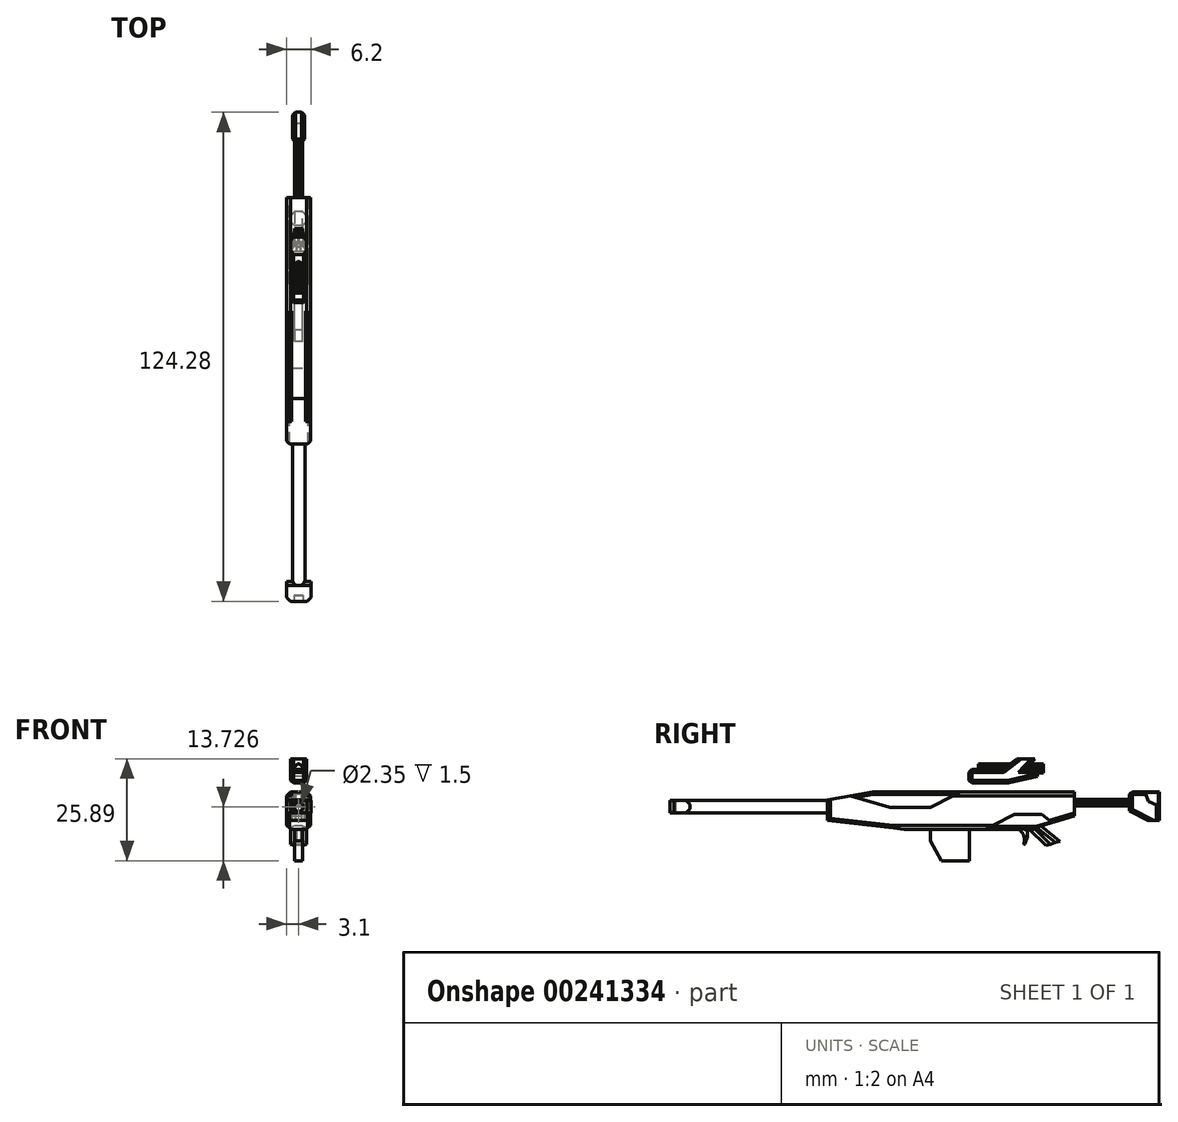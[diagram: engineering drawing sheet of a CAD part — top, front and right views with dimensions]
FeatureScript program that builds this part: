
annotation { "Feature Type Name" : "Feature", "Feature Type Description" : "" }
export const myFeature = defineFeature(function(context is Context, id is Id, definition is map)
    precondition{}
    {
        {
            var Q0;
            Q0=qCreatedBy(makeId("Right.planeOp"),FACE);
            var sketch = newSketch(context, id + "F0", { "sketchPlane" : qUnion([Q0])});
            skLineSegment(sketch, "E0.bottom", {"start": v(13.03, -2.2) * mm, "end": v(-18.93, -2.2) * mm});
            skLineSegment(sketch, "E0.top", {"start": v(24.37, 7.34) * mm, "end": v(-26.77, 7.34) * mm});
            skLineSegment(sketch, "E0.left", {"start": v(24.37, 1.22) * mm, "end": v(24.37, 7.34) * mm});
            skLineSegment(sketch, "E0.right", {"start": v(-38.28, 0) * mm, "end": v(-38.28, 5.3) * mm});
            skLineSegment(sketch, "E1.bottom", {"start": v(24.37, 5.38) * mm, "end": v(38.43, 5.38) * mm});
            skLineSegment(sketch, "E1.top", {"start": v(24.37, 3.77) * mm, "end": v(38.43, 3.77) * mm});
            skLineSegment(sketch, "E1.left", {"start": v(24.37, 5.38) * mm, "end": v(24.37, 3.77) * mm});
            skLineSegment(sketch, "E1.right", {"start": v(38.43, 5.38) * mm, "end": v(38.43, 3.77) * mm});
            skLineSegment(sketch, "E2.bottom", {"start": v(38.43, 7.34) * mm, "end": v(46, 7.34) * mm});
            skLineSegment(sketch, "E2.top", {"start": v(43.12, 0) * mm, "end": v(46, 0) * mm});
            skLineSegment(sketch, "E2.left", {"start": v(38.43, 7.34) * mm, "end": v(38.43, 2.48) * mm});
            skLineSegment(sketch, "E2.right", {"start": v(46, 7.34) * mm, "end": v(46, 0) * mm});
            skLineSegment(sketch, "E3", {"start": v(38.43, 2.48) * mm, "end": v(43.12, 0) * mm});
            skLineSegment(sketch, "E4", {"start": v(24.37, 1.22) * mm, "end": v(13.03, -2.2) * mm});
            skLineSegment(sketch, "E5", {"start": v(-26.77, 7.34) * mm, "end": v(-38.28, 5.3) * mm});
            skLineSegment(sketch, "E6", {"start": v(-18.93, -2.2) * mm, "end": v(-38.28, 0) * mm});
            skLineSegment(sketch, "E7", {"start": v(15.95, -1.32) * mm, "end": v(20.76, -5.24) * mm});
            skLineSegment(sketch, "E8", {"start": v(20.76, -5.24) * mm, "end": v(17.18, -6.32) * mm});
            skLineSegment(sketch, "E9", {"start": v(17.18, -6.32) * mm, "end": v(13.03, -2.2) * mm});
            skLineSegment(sketch, "E10", {"start": v(18.7, -0.49) * mm, "end": v(16.14, 1.57) * mm});
            skLineSegment(sketch, "E11", {"start": v(16.14, 1.57) * mm, "end": v(9.2, 1.57) * mm});
            skLineSegment(sketch, "E12", {"start": v(9.2, 1.57) * mm, "end": v(1.75, -2.2) * mm});
            skLineSegment(sketch, "E13", {"start": v(-4.55, 7.34) * mm, "end": v(-12.13, 3.37) * mm});
            skLineSegment(sketch, "E14", {"start": v(-12.13, 3.37) * mm, "end": v(-22.4, 3.37) * mm});
            skLineSegment(sketch, "E15", {"start": v(-22.4, 3.37) * mm, "end": v(-32.53, 6.32) * mm});
            skLineSegment(sketch, "E16", {"start": v(42.21, 7.34) * mm, "end": v(43.25, 4.9) * mm});
            skLineSegment(sketch, "E17", {"start": v(43.25, 4.9) * mm, "end": v(46, 3.67) * mm});
            skLineSegment(sketch, "E18.bottom", {"start": v(14.98, 13) * mm, "end": v(11.83, 13) * mm});
            skLineSegment(sketch, "E18.top", {"start": v(7.66, 9.53) * mm, "end": v(-2.36, 9.53) * mm});
            skLineSegment(sketch, "E18.left", {"start": v(14.98, 13) * mm, "end": v(14.98, 11.27) * mm});
            skLineSegment(sketch, "E18.right", {"start": v(-2.36, 13) * mm, "end": v(-2.36, 9.53) * mm});
            skLineSegment(sketch, "E19", {"start": v(14.98, 11.27) * mm, "end": v(7.66, 9.53) * mm});
            skLineSegment(sketch, "E20", {"start": v(11.83, 13) * mm, "end": v(14.34, 15.7) * mm});
            skLineSegment(sketch, "E21", {"start": v(14.34, 15.7) * mm, "end": v(9.84, 15.7) * mm});
            skLineSegment(sketch, "E22", {"start": v(9.84, 15.7) * mm, "end": v(6.3, 13) * mm});
            skLineSegment(sketch, "E23", {"start": v(8.08, 14.35) * mm, "end": v(0, 14.35) * mm});
            skLineSegment(sketch, "E24", {"start": v(0, 14.35) * mm, "end": v(0, 13) * mm});
            skPoint(sketch, "E25.orphan", {"position": v(14.98, 9.53) * mm});
            skLineSegment(sketch, "E26.trimOffspring", {"start": v(6.3, 13) * mm, "end": v(-2.36, 13) * mm});
            skLineSegment(sketch, "E27", {"start": v(13.08, 14.35) * mm, "end": v(16.5, 14.35) * mm});
            skLineSegment(sketch, "E28", {"start": v(16.5, 14.35) * mm, "end": v(16.5, 12.14) * mm});
            skLineSegment(sketch, "E29", {"start": v(16.5, 12.14) * mm, "end": v(14.98, 12.14) * mm});
            skFitSpline(sketch, "E30", {"points": [v(11.9, -2.2) * mm, v(12.5, -3.65) * mm, v(11.65, -6.06) * mm, v(11.53, -3.7) * mm, v(10.58, -2.2) * mm, v(11.9, -2.2) * mm]});
            skSolve(sketch);
        }
        {
            var Q0;
            {var subQ5=sQuery(id+"F0.wireOp",EDGE,"E0.right");Q0=makeQuery(id+"F0.imprint","IMPRINT",FACE,{"disambiguationData":[TD([[makeQuery(id+"F0.imprint","IMPRINT",EDGE,{"derivedFrom":subQ5}),-1.0]])]});}
            extrude(context, id + "F1", {"entities" : qUnion([Q0]), "oppositeDirection" : true, "depth" : 3 * mm});
        }
        {
            var Q0;
            {var subQ5=sQuery(id+"F0.wireOp",EDGE,"E0.right");Q0=makeQuery(id+"F0.imprint","IMPRINT",FACE,{"disambiguationData":[TD([[makeQuery(id+"F0.imprint","IMPRINT",EDGE,{"derivedFrom":subQ5}),-1.0]])]});}
            extrude(context, id + "F2", {"entities" : qUnion([Q0]), "operationType" : NewBodyOperationType.ADD, "depth" : 3 * mm});
        }
        {
            var Q0;
            {var subQ0=sQuery(id+"F0.wireOp",EDGE,"E13");Q0=makeQuery(id+"F0.imprint","IMPRINT",FACE,{"disambiguationData":[TD([[makeQuery(id+"F0.imprint","IMPRINT",EDGE,{"derivedFrom":subQ0}),-1.0]])]});}
            extrude(context, id + "F3", {"entities" : qUnion([Q0]), "operationType" : NewBodyOperationType.ADD, "oppositeDirection" : true, "depth" : 2.5 * mm});
        }
        {
            var Q0;
            {var subQ0=sQuery(id+"F0.wireOp",EDGE,"E13");Q0=makeQuery(id+"F0.imprint","IMPRINT",FACE,{"disambiguationData":[TD([[makeQuery(id+"F0.imprint","IMPRINT",EDGE,{"derivedFrom":subQ0}),-1.0]])]});}
            extrude(context, id + "F4", {"entities" : qUnion([Q0]), "operationType" : NewBodyOperationType.ADD, "depth" : 2.5 * mm});
        }
        {
            var Q0;
            {var subQ0=sQuery(id+"F0.wireOp",EDGE,"E10");Q0=makeQuery(id+"F0.imprint","IMPRINT",FACE,{"disambiguationData":[TD([[makeQuery(id+"F0.imprint","IMPRINT",EDGE,{"derivedFrom":subQ0}),1.0]])]});}
            extrude(context, id + "F5", {"entities" : qUnion([Q0]), "operationType" : NewBodyOperationType.ADD, "depth" : 2.5 * mm});
        }
        {
            var Q0;
            {var subQ0=sQuery(id+"F0.wireOp",EDGE,"E10");Q0=makeQuery(id+"F0.imprint","IMPRINT",FACE,{"disambiguationData":[TD([[makeQuery(id+"F0.imprint","IMPRINT",EDGE,{"derivedFrom":subQ0}),1.0]])]});}
            extrude(context, id + "F6", {"entities" : qUnion([Q0]), "operationType" : NewBodyOperationType.ADD, "oppositeDirection" : true, "depth" : 2.5 * mm});
        }
        {
            var Q0;
            {var subQ2=sQuery(id+"F0.wireOp",EDGE,"E7");Q0=makeQuery(id+"F0.imprint","IMPRINT",FACE,{"disambiguationData":[TD([[makeQuery(id+"F0.imprint","IMPRINT",EDGE,{"derivedFrom":subQ2}),-1.0]])]});}
            extrude(context, id + "F7", {"entities" : qUnion([Q0]), "operationType" : NewBodyOperationType.ADD, "depth" : 2 * mm});
        }
        {
            var Q0;
            {var subQ2=sQuery(id+"F0.wireOp",EDGE,"E7");Q0=makeQuery(id+"F0.imprint","IMPRINT",FACE,{"disambiguationData":[TD([[makeQuery(id+"F0.imprint","IMPRINT",EDGE,{"derivedFrom":subQ2}),-1.0]])]});}
            extrude(context, id + "F8", {"entities" : qUnion([Q0]), "operationType" : NewBodyOperationType.ADD, "oppositeDirection" : true, "depth" : 2 * mm});
        }
        {
            var Q0;
            {var subQ0=sQuery(id+"F0.wireOp",EDGE,"E1.bottom");Q0=makeQuery(id+"F0.imprint","IMPRINT",FACE,{"disambiguationData":[TD([[makeQuery(id+"F0.imprint","IMPRINT",EDGE,{"derivedFrom":subQ0}),-1.0]])]});}
            extrude(context, id + "F9", {"entities" : qUnion([Q0]), "operationType" : NewBodyOperationType.ADD, "depth" : 1 * mm});
        }
        {
            var Q0;
            {var subQ0=sQuery(id+"F0.wireOp",EDGE,"E1.bottom");Q0=makeQuery(id+"F0.imprint","IMPRINT",FACE,{"disambiguationData":[TD([[makeQuery(id+"F0.imprint","IMPRINT",EDGE,{"derivedFrom":subQ0}),-1.0]])]});}
            extrude(context, id + "F10", {"entities" : qUnion([Q0]), "operationType" : NewBodyOperationType.ADD, "oppositeDirection" : true, "depth" : 1 * mm});
        }
        {
            var Q0;
            {var subQ7=sQuery(id+"F0.wireOp",EDGE,"E2.top");Q0=makeQuery(id+"F0.imprint","IMPRINT",FACE,{"disambiguationData":[TD([[makeQuery(id+"F0.imprint","IMPRINT",EDGE,{"derivedFrom":subQ7}),1.0]])]});}
            extrude(context, id + "F11", {"entities" : qUnion([Q0]), "operationType" : NewBodyOperationType.ADD, "depth" : 1.5 * mm});
        }
        {
            var Q0;
            {var subQ7=sQuery(id+"F0.wireOp",EDGE,"E2.top");Q0=makeQuery(id+"F0.imprint","IMPRINT",FACE,{"disambiguationData":[TD([[makeQuery(id+"F0.imprint","IMPRINT",EDGE,{"derivedFrom":subQ7}),1.0]])]});}
            extrude(context, id + "F12", {"entities" : qUnion([Q0]), "operationType" : NewBodyOperationType.ADD, "oppositeDirection" : true, "depth" : 1.5 * mm});
        }
        {
            var Q0;
            {var subQ3=sQuery(id+"F0.wireOp",EDGE,"E16");Q0=makeQuery(id+"F0.imprint","IMPRINT",FACE,{"disambiguationData":[TD([[makeQuery(id+"F0.imprint","IMPRINT",EDGE,{"derivedFrom":subQ3}),1.0]])]});}
            extrude(context, id + "F13", {"entities" : qUnion([Q0]), "operationType" : NewBodyOperationType.ADD, "depth" : 1 * mm});
        }
        {
            var Q0;
            {var subQ3=sQuery(id+"F0.wireOp",EDGE,"E16");Q0=makeQuery(id+"F0.imprint","IMPRINT",FACE,{"disambiguationData":[TD([[makeQuery(id+"F0.imprint","IMPRINT",EDGE,{"derivedFrom":subQ3}),1.0]])]});}
            extrude(context, id + "F14", {"entities" : qUnion([Q0]), "operationType" : NewBodyOperationType.ADD, "oppositeDirection" : true, "depth" : 1 * mm});
        }
        {
            var Q0;
            Q0=makeQuery(id+"F0.imprint","IMPRINT",FACE,{"disambiguationData":[TD([[makeQuery(id+"F0.imprint","IMPRINT",EDGE,{"derivedFrom":sQuery(id+"F0.wireOp",EDGE,"E18.bottom")}),1.0]])]});
            extrude(context, id + "F15", {"entities" : qUnion([Q0]), "depth" : 2 * mm});
        }
        {
            var Q0;
            Q0=makeQuery(id+"F0.imprint","IMPRINT",FACE,{"disambiguationData":[TD([[makeQuery(id+"F0.imprint","IMPRINT",EDGE,{"derivedFrom":sQuery(id+"F0.wireOp",EDGE,"E18.bottom")}),1.0]])]});
            extrude(context, id + "F16", {"entities" : qUnion([Q0]), "operationType" : NewBodyOperationType.ADD, "oppositeDirection" : true, "depth" : 2 * mm});
        }
        {
            var Q0;
            {var subQ3=sQuery(id+"F0.wireOp",EDGE,"E23");Q0=makeQuery(id+"F0.imprint","IMPRINT",FACE,{"disambiguationData":[TD([[makeQuery(id+"F0.imprint","IMPRINT",EDGE,{"derivedFrom":subQ3}),1.0]])]});}
            var Q1;
            {var subQ1=sQuery(id+"F0.wireOp",EDGE,"E18.bottom");Q1=makeQuery(id+"F0.imprint","IMPRINT",FACE,{"disambiguationData":[TD([[makeQuery(id+"F0.imprint","IMPRINT",EDGE,{"derivedFrom":subQ1}),-1.0]])]});}
            extrude(context, id + "F17", {"entities" : qUnion([Q0, Q1]), "operationType" : NewBodyOperationType.ADD, "depth" : 1 * mm});
        }
        {
            var Q0;
            {var subQ3=sQuery(id+"F0.wireOp",EDGE,"E23");Q0=makeQuery(id+"F0.imprint","IMPRINT",FACE,{"disambiguationData":[TD([[makeQuery(id+"F0.imprint","IMPRINT",EDGE,{"derivedFrom":subQ3}),1.0]])]});}
            var Q1;
            {var subQ1=sQuery(id+"F0.wireOp",EDGE,"E18.bottom");Q1=makeQuery(id+"F0.imprint","IMPRINT",FACE,{"disambiguationData":[TD([[makeQuery(id+"F0.imprint","IMPRINT",EDGE,{"derivedFrom":subQ1}),-1.0]])]});}
            extrude(context, id + "F18", {"entities" : qUnion([Q0, Q1]), "operationType" : NewBodyOperationType.ADD, "oppositeDirection" : true, "depth" : 1 * mm});
        }
        {
            var Q0;
            Q0=makeQuery(id+"F10.opExtrude","CAP_EDGE",EDGE,{"disambiguationData":[OSD([sQuery(id+"F0.wireOp",EDGE,"E1.bottom")])],"isStart":false});
            var Q1;
            Q1=makeQuery(id+"F16.opExtrude","CAP_EDGE",EDGE,{"disambiguationData":[OSD([sQuery(id+"F0.wireOp",EDGE,"E26.trimOffspring")])],"isStart":false});
            var Q2;
            Q2=makeQuery(id+"F15.opExtrude","CAP_EDGE",EDGE,{"disambiguationData":[OSD([sQuery(id+"F0.wireOp",EDGE,"E26.trimOffspring")])],"isStart":false});
            var Q3;
            Q3=makeQuery(id+"F9.opExtrude","CAP_EDGE",EDGE,{"disambiguationData":[OSD([sQuery(id+"F0.wireOp",EDGE,"E1.bottom")])],"isStart":false});
            var Q4;
            Q4=makeQuery(id+"F10.opExtrude","CAP_EDGE",EDGE,{"disambiguationData":[OSD([sQuery(id+"F0.wireOp",EDGE,"E1.top")])],"isStart":false});
            var Q5;
            Q5=makeQuery(id+"F9.opExtrude","CAP_EDGE",EDGE,{"disambiguationData":[OSD([sQuery(id+"F0.wireOp",EDGE,"E1.top")])],"isStart":false});
            var Q6;
            Q6=makeQuery(id+"F11.opExtrude","CAP_EDGE",EDGE,{"disambiguationData":[OSD([sQuery(id+"F0.wireOp",EDGE,"E2.bottom")])],"isStart":false});
            var Q7;
            Q7=makeQuery(id+"F12.opExtrude","CAP_EDGE",EDGE,{"disambiguationData":[OSD([sQuery(id+"F0.wireOp",EDGE,"E2.bottom")])],"isStart":false});
            var Q8;
            Q8=makeQuery(id+"F12.opExtrude","CAP_EDGE",EDGE,{"disambiguationData":[OSD([sQuery(id+"F0.wireOp",EDGE,"E3")])],"isStart":false});
            var Q9;
            Q9=makeQuery(id+"F11.opExtrude","CAP_EDGE",EDGE,{"disambiguationData":[OSD([sQuery(id+"F0.wireOp",EDGE,"E3")])],"isStart":false});
            var Q10;
            Q10=makeQuery(id+"F11.opExtrude","CAP_EDGE",EDGE,{"disambiguationData":[OSD([sQuery(id+"F0.wireOp",EDGE,"E2.right")])],"isStart":false});
            var Q11;
            Q11=makeQuery(id+"F12.opExtrude","CAP_EDGE",EDGE,{"disambiguationData":[OSD([sQuery(id+"F0.wireOp",EDGE,"E2.right")])],"isStart":false});
            var Q12;
            Q12=makeQuery(id+"F16.opExtrude","CAP_EDGE",EDGE,{"disambiguationData":[OSD([sQuery(id+"F0.wireOp",EDGE,"E19")])],"isStart":false});
            var Q13;
            Q13=makeQuery(id+"F15.opExtrude","CAP_EDGE",EDGE,{"disambiguationData":[OSD([sQuery(id+"F0.wireOp",EDGE,"E18.top")])],"isStart":false});
            var Q14;
            Q14=makeQuery(id+"F15.opExtrude","CAP_EDGE",EDGE,{"disambiguationData":[OSD([sQuery(id+"F0.wireOp",EDGE,"E19")])],"isStart":false});
            var Q15;
            Q15=makeQuery(id+"F15.opExtrude","CAP_EDGE",EDGE,{"disambiguationData":[OSD([sQuery(id+"F0.wireOp",EDGE,"E18.bottom")])],"isStart":false});
            var Q16;
            Q16=makeQuery(id+"F15.opExtrude","CAP_EDGE",EDGE,{"disambiguationData":[OSD([sQuery(id+"F0.wireOp",EDGE,"E20")])],"isStart":false});
            var Q17;
            Q17=makeQuery(id+"F15.opExtrude","CAP_EDGE",EDGE,{"disambiguationData":[OSD([sQuery(id+"F0.wireOp",EDGE,"E22")])],"isStart":false});
            var Q18;
            Q18=makeQuery(id+"F16.opExtrude","CAP_EDGE",EDGE,{"disambiguationData":[OSD([sQuery(id+"F0.wireOp",EDGE,"E18.top")])],"isStart":false});
            var Q19;
            Q19=makeQuery(id+"F16.opExtrude","CAP_EDGE",EDGE,{"disambiguationData":[OSD([sQuery(id+"F0.wireOp",EDGE,"E18.right")])],"isStart":false});
            var Q20;
            Q20=makeQuery(id+"F15.opExtrude","CAP_EDGE",EDGE,{"disambiguationData":[OSD([sQuery(id+"F0.wireOp",EDGE,"E18.right")])],"isStart":false});
            var Q21;
            {var subQ0=sQuery(id+"F0.wireOp",EDGE,"E26.trimOffspring");var subQ1=sQuery(id+"F0.wireOp",EDGE,"E18.right");Q21=makeQuery(id+"F16.boolean.opBoolean","MERGE",EDGE,{"derivedFrom":[makeQuery(id+"F15.opExtrude","SWEPT_EDGE",EDGE,{"disambiguationData":[OSD([subQ1,subQ0])]}),makeQuery(id+"F16.opExtrude","SWEPT_EDGE",EDGE,{"disambiguationData":[OSD([subQ1,subQ0])]})]});}
            var Q22;
            {var subQ0=sQuery(id+"F0.wireOp",EDGE,"E18.right");var subQ1=sQuery(id+"F0.wireOp",EDGE,"E18.top");Q22=makeQuery(id+"F16.boolean.opBoolean","MERGE",EDGE,{"derivedFrom":[makeQuery(id+"F15.opExtrude","SWEPT_EDGE",EDGE,{"disambiguationData":[OSD([subQ1,subQ0])]}),makeQuery(id+"F16.opExtrude","SWEPT_EDGE",EDGE,{"disambiguationData":[OSD([subQ1,subQ0])]})]});}
            var Q23;
            Q23=makeQuery(id+"F16.opExtrude","CAP_EDGE",EDGE,{"disambiguationData":[OSD([sQuery(id+"F0.wireOp",EDGE,"E20")])],"isStart":false});
            var Q24;
            Q24=makeQuery(id+"F16.opExtrude","CAP_EDGE",EDGE,{"disambiguationData":[OSD([sQuery(id+"F0.wireOp",EDGE,"E22")])],"isStart":false});
            var Q25;
            Q25=makeQuery(id+"F16.opExtrude","CAP_EDGE",EDGE,{"disambiguationData":[OSD([sQuery(id+"F0.wireOp",EDGE,"E18.bottom")])],"isStart":false});
            var Q26;
            {var subQ0=sQuery(id+"F0.wireOp",EDGE,"E2.left");var subQ1=sQuery(id+"F0.wireOp",EDGE,"E2.bottom");Q26=makeQuery(id+"F12.boolean.opBoolean","MERGE",EDGE,{"derivedFrom":[makeQuery(id+"F11.opExtrude","SWEPT_EDGE",EDGE,{"disambiguationData":[OSD([subQ1,subQ0])]}),makeQuery(id+"F12.opExtrude","SWEPT_EDGE",EDGE,{"disambiguationData":[OSD([subQ1,subQ0])]})]});}
            chamfer(context, id + "F19", {"entities" : qUnion([Q0, Q1, Q2, Q3, Q4, Q5, Q6, Q7, Q8, Q9, Q10, Q11, Q12, Q13, Q14, Q15, Q16, Q17, Q18, Q19, Q20, Q21, Q22, Q23, Q24, Q25, Q26]), "width" : 0.7 * mm, "tangentPropagation" : true});
        }
        {
            var Q0;
            Q0=makeQuery(id+"F12.opExtrude","CAP_EDGE",EDGE,{"disambiguationData":[OSD([sQuery(id+"F0.wireOp",EDGE,"E2.left")])],"isStart":false});
            var Q1;
            Q1=makeQuery(id+"F11.opExtrude","CAP_EDGE",EDGE,{"disambiguationData":[OSD([sQuery(id+"F0.wireOp",EDGE,"E2.left")])],"isStart":false});
            var Q2;
            Q2=makeQuery(id+"F3.opExtrude","CAP_EDGE",EDGE,{"disambiguationData":[OSD([sQuery(id+"F0.wireOp",EDGE,"E0.top")])],"isStart":false});
            var Q3;
            Q3=makeQuery(id+"F3.opExtrude","CAP_EDGE",EDGE,{"disambiguationData":[OSD([sQuery(id+"F0.wireOp",EDGE,"E5")])],"isStart":false});
            var Q4;
            Q4=makeQuery(id+"F4.opExtrude","CAP_EDGE",EDGE,{"disambiguationData":[OSD([sQuery(id+"F0.wireOp",EDGE,"E5")])],"isStart":false});
            var Q5;
            Q5=makeQuery(id+"F4.opExtrude","CAP_EDGE",EDGE,{"disambiguationData":[OSD([sQuery(id+"F0.wireOp",EDGE,"E0.top")])],"isStart":false});
            var Q6;
            Q6=makeQuery(id+"F1.opExtrude","CAP_EDGE",EDGE,{"disambiguationData":[OSD([sQuery(id+"F0.wireOp",EDGE,"E0.right")])],"isStart":false});
            var Q7;
            Q7=makeQuery(id+"F2.opExtrude","CAP_EDGE",EDGE,{"disambiguationData":[OSD([sQuery(id+"F0.wireOp",EDGE,"E0.right")])],"isStart":false});
            var Q8;
            Q8=makeQuery(id+"F1.opExtrude","CAP_EDGE",EDGE,{"disambiguationData":[OSD([sQuery(id+"F0.wireOp",EDGE,"E6")])],"isStart":false});
            var Q9;
            Q9=makeQuery(id+"F2.opExtrude","CAP_EDGE",EDGE,{"disambiguationData":[OSD([sQuery(id+"F0.wireOp",EDGE,"E6")])],"isStart":false});
            var Q10;
            Q10=makeQuery(id+"F6.opExtrude","CAP_EDGE",EDGE,{"disambiguationData":[OSD([sQuery(id+"F0.wireOp",EDGE,"E0.bottom")])],"isStart":false});
            var Q11;
            Q11=makeQuery(id+"F5.opExtrude","CAP_EDGE",EDGE,{"disambiguationData":[OSD([sQuery(id+"F0.wireOp",EDGE,"E0.bottom")])],"isStart":false});
            var Q12;
            Q12=makeQuery(id+"F1.opExtrude","CAP_EDGE",EDGE,{"disambiguationData":[OSD([sQuery(id+"F0.wireOp",EDGE,"E4")])],"isStart":false});
            var Q13;
            Q13=makeQuery(id+"F2.opExtrude","CAP_EDGE",EDGE,{"disambiguationData":[OSD([sQuery(id+"F0.wireOp",EDGE,"E4")])],"isStart":false});
            chamfer(context, id + "F20", {"entities" : qUnion([Q0, Q1, Q2, Q3, Q4, Q5, Q6, Q7, Q8, Q9, Q10, Q11, Q12, Q13]), "width" : 0.7 * mm, "tangentPropagation" : true});
        }
        {
            var Q0;
            Q0=makeQuery(id+"F1.opExtrude","CAP_EDGE",EDGE,{"disambiguationData":[OSD([sQuery(id+"F0.wireOp",EDGE,"E0.top")])],"isStart":false});
            var Q1;
            Q1=makeQuery(id+"F2.opExtrude","CAP_EDGE",EDGE,{"disambiguationData":[OSD([sQuery(id+"F0.wireOp",EDGE,"E0.top")])],"isStart":false});
            var Q2;
            Q2=makeQuery(id+"F1.opExtrude","CAP_EDGE",EDGE,{"disambiguationData":[OSD([sQuery(id+"F0.wireOp",EDGE,"E0.bottom")])],"isStart":false});
            var Q3;
            Q3=makeQuery(id+"F2.opExtrude","CAP_EDGE",EDGE,{"disambiguationData":[OSD([sQuery(id+"F0.wireOp",EDGE,"E0.bottom")])],"isStart":false});
            var Q4;
            Q4=makeQuery(id+"F8.opExtrude","CAP_EDGE",EDGE,{"disambiguationData":[OSD([sQuery(id+"F0.wireOp",EDGE,"E9")])],"isStart":false});
            var Q5;
            Q5=makeQuery(id+"F8.opExtrude","CAP_EDGE",EDGE,{"disambiguationData":[OSD([sQuery(id+"F0.wireOp",EDGE,"E7")])],"isStart":false});
            var Q6;
            Q6=makeQuery(id+"F7.opExtrude","CAP_EDGE",EDGE,{"disambiguationData":[OSD([sQuery(id+"F0.wireOp",EDGE,"E9")])],"isStart":false});
            var Q7;
            Q7=makeQuery(id+"F7.opExtrude","CAP_EDGE",EDGE,{"disambiguationData":[OSD([sQuery(id+"F0.wireOp",EDGE,"E7")])],"isStart":false});
            chamfer(context, id + "F21", {"entities" : qUnion([Q0, Q1, Q2, Q3, Q4, Q5, Q6, Q7]), "width" : 1 * mm, "tangentPropagation" : true});
        }
        {
            var Q0;
            Q0=makeQuery(id+"F18.opExtrude","CAP_EDGE",EDGE,{"disambiguationData":[OSD([sQuery(id+"F0.wireOp",EDGE,"E27")])],"isStart":false});
            var Q1;
            Q1=makeQuery(id+"F17.opExtrude","CAP_EDGE",EDGE,{"disambiguationData":[OSD([sQuery(id+"F0.wireOp",EDGE,"E27")])],"isStart":false});
            var Q2;
            Q2=makeQuery(id+"F18.opExtrude","CAP_EDGE",EDGE,{"disambiguationData":[OSD([sQuery(id+"F0.wireOp",EDGE,"E29")])],"isStart":false});
            var Q3;
            Q3=makeQuery(id+"F17.opExtrude","CAP_EDGE",EDGE,{"disambiguationData":[OSD([sQuery(id+"F0.wireOp",EDGE,"E29")])],"isStart":false});
            var Q4;
            Q4=makeQuery(id+"F17.opExtrude","CAP_EDGE",EDGE,{"disambiguationData":[OSD([sQuery(id+"F0.wireOp",EDGE,"E23")])],"isStart":false});
            var Q5;
            Q5=makeQuery(id+"F18.opExtrude","CAP_EDGE",EDGE,{"disambiguationData":[OSD([sQuery(id+"F0.wireOp",EDGE,"E23")])],"isStart":false});
            chamfer(context, id + "F22", {"entities" : qUnion([Q0, Q1, Q2, Q3, Q4, Q5]), "width" : 0.7 * mm, "tangentPropagation" : true});
        }
        {
            var Q0;
            {var subQ0=sQuery(id+"F0.wireOp",EDGE,"E0.right");Q0=makeQuery(id+"F2.boolean.opBoolean","MERGE",FACE,{"derivedFrom":[makeQuery(id+"F1.opExtrude","SWEPT_FACE",FACE,{"disambiguationData":[OSD([subQ0])]}),makeQuery(id+"F2.opExtrude","SWEPT_FACE",FACE,{"disambiguationData":[OSD([subQ0])]})]});}
            var sketch = newSketch(context, id + "F23", { "sketchPlane" : qUnion([Q0])});
            skCircle(sketch, "E31", {"center": v(0, 3.54) * mm, "radius": 1.57 * mm});
            skSolve(sketch);
        }
        {
            var Q0;
            Q0=makeQuery(id+"F23.imprint","IMPRINT",FACE,{"disambiguationData":[TD([[makeQuery(id+"F23.imprint","IMPRINT",EDGE,{"derivedFrom":sQuery(id+"F23.wireOp",EDGE,"E31")}),1.0]])]});
            extrude(context, id + "F24", {"entities" : qUnion([Q0]), "operationType" : NewBodyOperationType.ADD, "depth" : 35 * mm});
        }
        {
            var Q0;
            {var subQ0=sQuery(id+"F0.wireOp",EDGE,"E0.bottom");Q0=makeQuery(id+"F6.boolean.opBoolean","MERGE",FACE,{"derivedFrom":[makeQuery(id+"F5.boolean.opBoolean","MERGE",FACE,{"derivedFrom":[makeQuery(id+"F2.boolean.opBoolean","MERGE",FACE,{"derivedFrom":[makeQuery(id+"F1.opExtrude","SWEPT_FACE",FACE,{"disambiguationData":[OSD([subQ0])]}),makeQuery(id+"F2.opExtrude","SWEPT_FACE",FACE,{"disambiguationData":[OSD([subQ0])]})]}),makeQuery(id+"F5.opExtrude","SWEPT_FACE",FACE,{"disambiguationData":[OSD([subQ0])]})]}),makeQuery(id+"F6.opExtrude","SWEPT_FACE",FACE,{"disambiguationData":[OSD([subQ0])]})]});}
            var sketch = newSketch(context, id + "F25", { "sketchPlane" : qUnion([Q0])});
            skLineSegment(sketch, "E32", {"start": v(0, 12.2) * mm, "end": v(-1, 12.2) * mm});
            skLineSegment(sketch, "E33.bottom", {"start": v(-1, 12.2) * mm, "end": v(1, 12.2) * mm});
            skLineSegment(sketch, "E33.top", {"start": v(-1, 2.2) * mm, "end": v(1, 2.2) * mm});
            skLineSegment(sketch, "E33.left", {"start": v(-1, 12.2) * mm, "end": v(-1, 2.2) * mm});
            skLineSegment(sketch, "E33.right", {"start": v(1, 12.2) * mm, "end": v(1, 2.2) * mm});
            skSolve(sketch);
        }
        {
            var Q0;
            Q0=makeQuery(id+"F25.imprint","IMPRINT",FACE,{"disambiguationData":[TD([[makeQuery(id+"F25.imprint","IMPRINT",EDGE,{"derivedFrom":sQuery(id+"F25.wireOp",EDGE,"E33.top")}),1.0]])]});
            extrude(context, id + "F26", {"entities" : qUnion([Q0]), "operationType" : NewBodyOperationType.ADD, "depth" : 8 * mm});
        }
        {
            var Q0;
            Q0=makeQuery(id+"F26.opExtrude","CAP_EDGE",EDGE,{"disambiguationData":[OSD([sQuery(id+"F25.wireOp",EDGE,"E33.bottom")])],"isStart":false});
            chamfer(context, id + "F27", {"entities" : qUnion([Q0]), "chamferType" : ChamferType.OFFSET_ANGLE, "width" : 5 * mm, "oppositeDirection" : true, "angle" : 30 * degree, "tangentPropagation" : true});
        }
        {
            var Q0;
            Q0=makeQuery(id+"F24.opExtrude","CAP_FACE",FACE,{"disambiguationData":[OSD([sQuery(id+"F23.wireOp",EDGE,"E31")])],"isStart":false});
            var sketch = newSketch(context, id + "F28", { "sketchPlane" : qUnion([Q0])});
            skLineSegment(sketch, "E34", {"start": v(0, 5.1) * mm, "end": v(-3.1, 5.1) * mm});
            skLineSegment(sketch, "E35", {"start": v(0, 1.96) * mm, "end": v(-3.1, 1.96) * mm});
            skLineSegment(sketch, "E36", {"start": v(-3.1, 1.96) * mm, "end": v(-3.1, 5.1) * mm});
            skLineSegment(sketch, "E37.MirrorCS", {"start": v(3.1, 1.96) * mm, "end": v(3.1, 5.1) * mm});
            skLineSegment(sketch, "E38.MirrorCS", {"start": v(0, 5.1) * mm, "end": v(3.1, 5.1) * mm});
            skLineSegment(sketch, "E39.MirrorCS", {"start": v(0, 1.96) * mm, "end": v(3.1, 1.96) * mm});
            skSolve(sketch);
        }
        {
            var Q0;
            {var subQ0=sQuery(id+"F28.wireOp",EDGE,"E34");Q0=makeQuery(id+"F28.imprint","IMPRINT",FACE,{"disambiguationData":[TD([[makeQuery(id+"F28.imprint","IMPRINT",EDGE,{"derivedFrom":subQ0}),1.0]])]});}
            var Q1;
            {var subQ0=makeQuery(id+"F24.opExtrude","CAP_EDGE",EDGE,{"disambiguationData":[OSD([sQuery(id+"F23.wireOp",EDGE,"E31")])],"isStart":false});var subQ1=makeQuery(id+"F28.imprint","INTERSECT",VERTEX,{"derivedFrom":[subQ0,sQuery(id+"F28.wireOp",EDGE,"E34"),sQuery(id+"F28.wireOp",EDGE,"E38.MirrorCS")]});Q1=makeQuery(id+"F28.imprint","IMPRINT",FACE,{"disambiguationData":[TD([[makeQuery(id+"F28.imprint","IMPRINT",EDGE,{"disambiguationData":[TD([[subQ1,-1.0]])],"derivedFrom":subQ0}),1.0]])]});}
            var Q2;
            Q2=makeQuery(id+"F28.imprint","IMPRINT",FACE,{"disambiguationData":[TD([[makeQuery(id+"F28.imprint","IMPRINT",EDGE,{"derivedFrom":sQuery(id+"F28.wireOp",EDGE,"E37.MirrorCS")}),1.0]])]});
            extrude(context, id + "F29", {"entities" : qUnion([Q0, Q1, Q2]), "operationType" : NewBodyOperationType.ADD, "depth" : 5 * mm});
        }
        {
            var Q0;
            {var subQ0=sQuery(id+"F28.wireOp",EDGE,"E38.MirrorCS");var subQ1=sQuery(id+"F28.wireOp",EDGE,"E36");var subQ2=sQuery(id+"F28.wireOp",EDGE,"E34");Q0=makeQuery(id+"F29.boolean.opBoolean","SPLIT",EDGE,{"disambiguationData":[TD([makeQuery(id+"F29.opExtrude","SWEPT_FACE",FACE,{"disambiguationData":[OSD([subQ1])]})])],"derivedFrom":makeQuery(id+"F29.opExtrude","CAP_EDGE",EDGE,{"disambiguationData":[OSD([subQ2,subQ0])],"isStart":true})});}
            var Q1;
            {var subQ0=sQuery(id+"F28.wireOp",EDGE,"E39.MirrorCS");var subQ1=sQuery(id+"F28.wireOp",EDGE,"E36");var subQ2=sQuery(id+"F28.wireOp",EDGE,"E35");Q1=makeQuery(id+"F29.boolean.opBoolean","SPLIT",EDGE,{"disambiguationData":[TD([makeQuery(id+"F29.opExtrude","SWEPT_FACE",FACE,{"disambiguationData":[OSD([subQ1])]})])],"derivedFrom":makeQuery(id+"F29.opExtrude","CAP_EDGE",EDGE,{"disambiguationData":[OSD([subQ2,subQ0])],"isStart":true})});}
            var Q2;
            Q2=makeQuery(id+"F29.opExtrude","CAP_EDGE",EDGE,{"disambiguationData":[OSD([sQuery(id+"F28.wireOp",EDGE,"E36")])],"isStart":false});
            var Q3;
            Q3=makeQuery(id+"F29.opExtrude","CAP_EDGE",EDGE,{"disambiguationData":[OSD([sQuery(id+"F28.wireOp",EDGE,"E37.MirrorCS")])],"isStart":false});
            chamfer(context, id + "F30", {"entities" : qUnion([Q0, Q1, Q2, Q3]), "width" : 1 * mm, "tangentPropagation" : true});
        }
        {
            var Q0;
            Q0=makeQuery(id+"F29.opExtrude","CAP_FACE",FACE,{"disambiguationData":[OSD([sQuery(id+"F28.wireOp",EDGE,"E34"),sQuery(id+"F28.wireOp",EDGE,"E35"),sQuery(id+"F28.wireOp",EDGE,"E36"),sQuery(id+"F28.wireOp",EDGE,"E37.MirrorCS"),sQuery(id+"F28.wireOp",EDGE,"E38.MirrorCS"),sQuery(id+"F28.wireOp",EDGE,"E39.MirrorCS")])],"isStart":false});
            var sketch = newSketch(context, id + "F31", { "sketchPlane" : qUnion([Q0])});
            skPoint(sketch, "E40.endSnap0", {"position": v(2.1, 3.54) * mm});
            skPoint(sketch, "E40.endSnap1", {"position": v(0, 1.96) * mm});
            skCircle(sketch, "E41", {"center": v(0, 3.54) * mm, "radius": 1.17 * mm});
            skPoint(sketch, "E42.orphan", {"position": v(0, 5.1) * mm});
            skSolve(sketch);
        }
        {
            var Q0;
            Q0=makeQuery(id+"F31.imprint","IMPRINT",FACE,{"disambiguationData":[TD([[makeQuery(id+"F31.imprint","IMPRINT",EDGE,{"derivedFrom":sQuery(id+"F31.wireOp",EDGE,"E41")}),1.0]])]});
            extrude(context, id + "F32", {"entities" : qUnion([Q0]), "operationType" : NewBodyOperationType.REMOVE, "oppositeDirection" : true, "depth" : 1.5 * mm});
        }
        {
            var Q0;
            {var subQ0=sQuery(id+"F0.wireOp",EDGE,"E30");Q0=makeQuery(id+"F0.imprint","IMPRINT",FACE,{"disambiguationData":[TD([[makeQuery(id+"F0.imprint","IMPRINT",EDGE,{"derivedFrom":subQ0}),-1.0]])]});}
            extrude(context, id + "F33", {"entities" : qUnion([Q0]), "operationType" : NewBodyOperationType.ADD, "depth" : 0.5 * mm});
        }
        {
            var Q0;
            {var subQ0=sQuery(id+"F0.wireOp",EDGE,"E30");Q0=makeQuery(id+"F0.imprint","IMPRINT",FACE,{"disambiguationData":[TD([[makeQuery(id+"F0.imprint","IMPRINT",EDGE,{"derivedFrom":subQ0}),-1.0]])]});}
            extrude(context, id + "F34", {"entities" : qUnion([Q0]), "operationType" : NewBodyOperationType.ADD, "oppositeDirection" : true, "depth" : 0.5 * mm});
        }
    });
